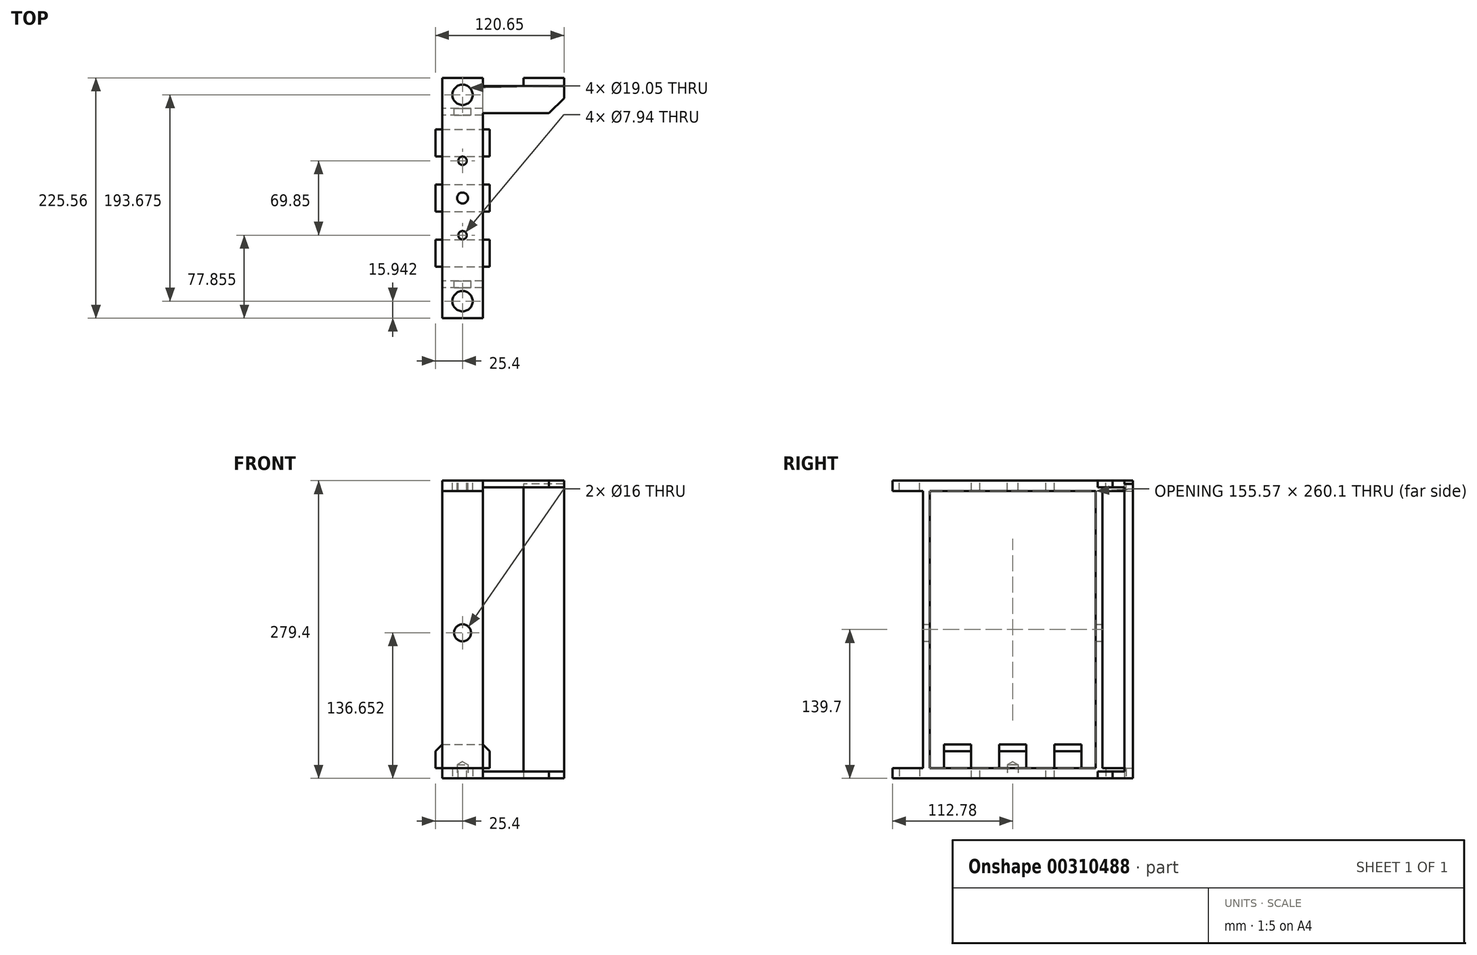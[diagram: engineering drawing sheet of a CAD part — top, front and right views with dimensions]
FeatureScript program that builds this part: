
annotation { "Feature Type Name" : "Feature", "Feature Type Description" : "" }
export const myFeature = defineFeature(function(context is Context, id is Id, definition is map)
    precondition{}
    {
        {
            var Q0;
            Q0=qCreatedBy(makeId("Right.planeOp"),FACE);
            var sketch = newSketch(context, id + "F0", { "sketchPlane" : qUnion([Q0])});
            skLineSegment(sketch, "E0.bottom", {"start": v(-112.78, 139.7) * mm, "end": v(112.78, 139.7) * mm, "construction": true});
            skLineSegment(sketch, "E0.top", {"start": v(-112.78, -139.7) * mm, "end": v(112.78, -139.7) * mm, "construction": true});
            skLineSegment(sketch, "E0.left", {"start": v(-112.78, 139.7) * mm, "end": v(-112.78, -139.7) * mm, "construction": true});
            skLineSegment(sketch, "E0.right", {"start": v(112.78, 139.7) * mm, "end": v(112.78, -139.7) * mm, "construction": true});
            skPoint(sketch, "E0.middle", {"position": v(0, 0) * mm});
            skLineSegment(sketch, "E1.bottom", {"start": v(-112.78, 139.7) * mm, "end": v(112.78, 139.7) * mm});
            skLineSegment(sketch, "E1.top", {"start": v(-112.78, 130.05) * mm, "end": v(112.78, 130.05) * mm});
            skLineSegment(sketch, "E1.left", {"start": v(-112.78, 139.7) * mm, "end": v(-112.78, 130.05) * mm});
            skLineSegment(sketch, "E1.right", {"start": v(112.78, 139.7) * mm, "end": v(112.78, 130.05) * mm});
            skLineSegment(sketch, "E2", {"start": v(-207.6, 0) * mm, "end": v(204.57, 0) * mm, "construction": true});
            skSolve(sketch);
        }
        {
            var Q0;
            Q0=qSketchRegion(id+"F0",true);
            extrude(context, id + "F1", {"entities" : qUnion([Q0]), "endBound" : BoundingType.SYMMETRIC, "depth" : 38.1 * mm});
        }
        {
            var Q0;
            Q0=makeQuery(id+"F1.opExtrude","SWEPT_FACE",FACE,{"disambiguationData":[OSD([sQuery(id+"F0.wireOp",EDGE,"E1.bottom")])]});
            var sketch = newSketch(context, id + "F2", { "sketchPlane" : qUnion([Q0])});
            skLineSegment(sketch, "E3", {"start": v(0, -177.25) * mm, "end": v(0, 167.17) * mm, "construction": true});
            skLineSegment(sketch, "E4", {"start": v(-122.09, 0) * mm, "end": v(96.88, 0) * mm, "construction": true});
            skLineSegment(sketch, "E5.0", {"start": v(-122.09, -96.84) * mm, "end": v(96.88, -96.84) * mm, "construction": true});
            skPoint(sketch, "E6", {"position": v(0, -96.84) * mm});
            skPoint(sketch, "E7.MirrorP", {"position": v(0, 96.84) * mm});
            skSolve(sketch);
        }
        {
            var Q0;
            Q0=sQuery(id+"F2.wireOp",VERTEX,"E6");
            var Q1;
            Q1=sQuery(id+"F2.wireOp",VERTEX,"E7.MirrorP");
            var Q2;
            Q2=makeQuery(id+"F1.opExtrude","SWEPT_BODY",BODY,{"disambiguationData":[OSD([sQuery(id+"F0.wireOp",EDGE,"E1.bottom"),sQuery(id+"F0.wireOp",EDGE,"E1.top"),sQuery(id+"F0.wireOp",EDGE,"E1.left"),sQuery(id+"F0.wireOp",EDGE,"E1.right")])]});
            hole(context, id + "F3", {"style" : HoleStyle.SIMPLE, "endStyle" : HoleEndStyle.THROUGH, "holeDiameter" : 19.05 * mm, "tappedDepth" : 24.13 * mm, "tapClearance" : 3, "startFromSketch" : true, "locations" : qUnion([Q0, Q1]), "scope" : qUnion([Q2])});
        }
        {
            var Q0;
            Q0=makeQuery(id+"F1.opExtrude","SWEPT_BODY",BODY,{"disambiguationData":[OSD([sQuery(id+"F0.wireOp",EDGE,"E1.bottom"),sQuery(id+"F0.wireOp",EDGE,"E1.top"),sQuery(id+"F0.wireOp",EDGE,"E1.left"),sQuery(id+"F0.wireOp",EDGE,"E1.right")])]});
            var Q1;
            Q1=qCreatedBy(makeId("Top.planeOp"),FACE);
            mirror(context, id + "F4", {"entities" : qUnion([Q0]), "mirrorPlane" : qUnion([Q1])});
        }
        {
            var Q0;
            Q0=qCreatedBy(makeId("Right.planeOp"),FACE);
            var sketch = newSketch(context, id + "F5", { "sketchPlane" : qUnion([Q0])});
            skLineSegment(sketch, "E8", {"start": v(0, 150.78) * mm, "end": v(0, -158.23) * mm, "construction": true});
            skLineSegment(sketch, "E9.0", {"start": v(-77.79, 150.78) * mm, "end": v(-77.79, -158.23) * mm, "construction": true});
            skLineSegment(sketch, "E10.0", {"start": v(-112.78, 130.05) * mm, "end": v(112.78, 130.05) * mm, "construction": true});
            skLineSegment(sketch, "E11.0", {"start": v(-112.78, -130.05) * mm, "end": v(112.78, -130.05) * mm, "construction": true});
            skLineSegment(sketch, "E12.bottom", {"start": v(-77.79, 130.05) * mm, "end": v(-84.14, 130.05) * mm});
            skLineSegment(sketch, "E12.top", {"start": v(-77.79, -130.05) * mm, "end": v(-84.14, -130.05) * mm});
            skLineSegment(sketch, "E12.left", {"start": v(-77.79, 130.05) * mm, "end": v(-77.79, -130.05) * mm});
            skLineSegment(sketch, "E12.right", {"start": v(-84.14, 130.05) * mm, "end": v(-84.14, -130.05) * mm});
            skLineSegment(sketch, "E13.MirrorCS", {"start": v(77.79, 130.05) * mm, "end": v(84.14, 130.05) * mm});
            skLineSegment(sketch, "E14.MirrorCS", {"start": v(77.79, -130.05) * mm, "end": v(84.14, -130.05) * mm});
            skLineSegment(sketch, "E15.MirrorCS", {"start": v(77.79, 130.05) * mm, "end": v(77.79, -130.05) * mm});
            skLineSegment(sketch, "E16.MirrorCS", {"start": v(84.14, 130.05) * mm, "end": v(84.14, -130.05) * mm});
            skLineSegment(sketch, "E17.MirrorCS", {"start": v(77.79, 150.78) * mm, "end": v(77.79, -158.23) * mm, "construction": true});
            skSolve(sketch);
        }
        {
            var Q0;
            Q0=qSketchRegion(id+"F5",true);
            extrude(context, id + "F6", {"entities" : qUnion([Q0]), "endBound" : BoundingType.SYMMETRIC, "depth" : 38.1 * mm});
        }
        {
            var Q0;
            Q0=makeQuery(id+"F6.opExtrude","SWEPT_FACE",FACE,{"disambiguationData":[OSD([sQuery(id+"F5.wireOp",EDGE,"E16.MirrorCS")])]});
            var sketch = newSketch(context, id + "F7", { "sketchPlane" : qUnion([Q0])});
            skLineSegment(sketch, "E18.0", {"start": v(-92.9, -130.05) * mm, "end": v(19.05, -130.05) * mm, "construction": true});
            skPoint(sketch, "E19.orphan", {"position": v(-19.05, -130.05) * mm});
            skLineSegment(sketch, "E20", {"start": v(0, 168.5) * mm, "end": v(0, -166.5) * mm, "construction": true});
            skLineSegment(sketch, "E21.0", {"start": v(-92.9, -3.05) * mm, "end": v(19.05, -3.05) * mm, "construction": true});
            skPoint(sketch, "E22", {"position": v(0, -3.05) * mm});
            skSolve(sketch);
        }
        {
            var Q0;
            Q0=makeQuery(id+"F1.opExtrude","SWEPT_BODY",BODY,{"disambiguationData":[OSD([sQuery(id+"F0.wireOp",EDGE,"E1.bottom"),sQuery(id+"F0.wireOp",EDGE,"E1.top"),sQuery(id+"F0.wireOp",EDGE,"E1.left"),sQuery(id+"F0.wireOp",EDGE,"E1.right")])]});
            var Q1;
            Q1=makeQuery(id+"F6.opExtrude","SWEPT_BODY",BODY,{"disambiguationData":[OSD([sQuery(id+"F5.wireOp",EDGE,"E12.bottom"),sQuery(id+"F5.wireOp",EDGE,"E12.top"),sQuery(id+"F5.wireOp",EDGE,"E12.left"),sQuery(id+"F5.wireOp",EDGE,"E12.right")])]});
            var Q2;
            Q2=makeQuery(id+"F6.opExtrude","SWEPT_BODY",BODY,{"disambiguationData":[OSD([sQuery(id+"F5.wireOp",EDGE,"E13.MirrorCS"),sQuery(id+"F5.wireOp",EDGE,"E14.MirrorCS"),sQuery(id+"F5.wireOp",EDGE,"E15.MirrorCS"),sQuery(id+"F5.wireOp",EDGE,"E16.MirrorCS")])]});
            var Q3;
            Q3=makeQuery(id+"F4.opPattern","COPY",BODY,{"derivedFrom":makeQuery(id+"F1.opExtrude","SWEPT_BODY",BODY,{"disambiguationData":[OSD([sQuery(id+"F0.wireOp",EDGE,"E1.bottom"),sQuery(id+"F0.wireOp",EDGE,"E1.top"),sQuery(id+"F0.wireOp",EDGE,"E1.left"),sQuery(id+"F0.wireOp",EDGE,"E1.right")])]}),"instanceName":"1"});
            booleanBodies(context, id + "F8", {"operationType" : BooleanOperationType.UNION, "tools" : qUnion([Q0, Q1, Q2, Q3])});
        }
        {
            var Q0;
            Q0=sQuery(id+"F7.wireOp",VERTEX,"E22");
            var Q1;
            Q1=makeQuery(id+"F1.opExtrude","SWEPT_BODY",BODY,{"disambiguationData":[OSD([sQuery(id+"F0.wireOp",EDGE,"E1.bottom"),sQuery(id+"F0.wireOp",EDGE,"E1.top"),sQuery(id+"F0.wireOp",EDGE,"E1.left"),sQuery(id+"F0.wireOp",EDGE,"E1.right")])]});
            hole(context, id + "F9", {"style" : HoleStyle.SIMPLE, "endStyle" : HoleEndStyle.THROUGH, "holeDiameter" : 16 * mm, "tappedDepth" : 24.13 * mm, "tapClearance" : 3, "startFromSketch" : true, "locations" : qUnion([Q0]), "scope" : qUnion([Q1])});
        }
        {
            var Q0;
            {var subQ2=sQuery(id+"F0.wireOp",EDGE,"E1.top");var subQ7=sQuery(id+"F5.wireOp",EDGE,"E12.left");Q0=makeQuery(id+"F8.opBoolean","SPLIT",FACE,{"disambiguationData":[TD([makeQuery(id+"F6.opExtrude","SWEPT_FACE",FACE,{"disambiguationData":[OSD([subQ7])]})])],"derivedFrom":makeQuery(id+"F4.opPattern","COPY",FACE,{"derivedFrom":makeQuery(id+"F1.opExtrude","SWEPT_FACE",FACE,{"disambiguationData":[OSD([subQ2])]}),"instanceName":"1"})});}
            var sketch = newSketch(context, id + "F10", { "sketchPlane" : qUnion([Q0])});
            skLineSegment(sketch, "E23", {"start": v(-127.69, 0) * mm, "end": v(108.08, 0) * mm, "construction": true});
            skLineSegment(sketch, "E24", {"start": v(0, -187.89) * mm, "end": v(0, 187.89) * mm, "construction": true});
            skLineSegment(sketch, "E25.0", {"start": v(-127.69, -51.69) * mm, "end": v(108.08, -51.69) * mm, "construction": true});
            skLineSegment(sketch, "E26.bottom", {"start": v(-25.4, -64.39) * mm, "end": v(25.4, -64.39) * mm});
            skLineSegment(sketch, "E26.top", {"start": v(-25.4, -38.99) * mm, "end": v(25.4, -38.99) * mm});
            skLineSegment(sketch, "E26.left", {"start": v(-25.4, -64.39) * mm, "end": v(-25.4, -38.99) * mm});
            skLineSegment(sketch, "E26.right", {"start": v(25.4, -64.39) * mm, "end": v(25.4, -38.99) * mm});
            skPoint(sketch, "E26.middle", {"position": v(0, -51.69) * mm});
            skLineSegment(sketch, "E27.0.1.0", {"start": v(-25.4, -12.7) * mm, "end": v(25.4, -12.7) * mm});
            skLineSegment(sketch, "E27.0.1.1", {"start": v(-25.4, 12.7) * mm, "end": v(25.4, 12.7) * mm});
            skLineSegment(sketch, "E27.0.1.2", {"start": v(-25.4, -12.7) * mm, "end": v(-25.4, 12.7) * mm});
            skLineSegment(sketch, "E27.0.1.3", {"start": v(25.4, -12.7) * mm, "end": v(25.4, 12.7) * mm});
            skPoint(sketch, "E27.0.1.4", {"position": v(0, 0) * mm});
            skLineSegment(sketch, "E27.0.2.0", {"start": v(-25.4, 38.99) * mm, "end": v(25.4, 38.99) * mm});
            skLineSegment(sketch, "E27.0.2.1", {"start": v(-25.4, 64.39) * mm, "end": v(25.4, 64.39) * mm});
            skLineSegment(sketch, "E27.0.2.2", {"start": v(-25.4, 38.99) * mm, "end": v(-25.4, 64.39) * mm});
            skLineSegment(sketch, "E27.0.2.3", {"start": v(25.4, 38.99) * mm, "end": v(25.4, 64.39) * mm});
            skPoint(sketch, "E27.0.2.4", {"position": v(0, 51.69) * mm});
            skLineSegment(sketch, "E27.direction1", {"start": v(-25.4, -64.39) * mm, "end": v(0, -64.39) * mm, "construction": true});
            skLineSegment(sketch, "E27.direction2", {"start": v(-25.4, -64.39) * mm, "end": v(-25.4, -12.7) * mm, "construction": true});
            skSolve(sketch);
        }
        {
            var Q0;
            Q0=qSketchRegion(id+"F10",true);
            extrude(context, id + "F11", {"entities" : qUnion([Q0]), "operationType" : NewBodyOperationType.ADD, "depth" : 22.35 * mm});
        }
        {
            var Q0;
            Q0=makeQuery(id+"F11.opExtrude","CAP_EDGE",EDGE,{"disambiguationData":[OSD([sQuery(id+"F10.wireOp",EDGE,"E26.left")])],"isStart":false});
            var Q1;
            Q1=makeQuery(id+"F11.opExtrude","CAP_EDGE",EDGE,{"disambiguationData":[OSD([sQuery(id+"F10.wireOp",EDGE,"E27.0.1.2")])],"isStart":false});
            var Q2;
            Q2=makeQuery(id+"F11.opExtrude","CAP_EDGE",EDGE,{"disambiguationData":[OSD([sQuery(id+"F10.wireOp",EDGE,"E27.0.2.2")])],"isStart":false});
            var Q3;
            Q3=makeQuery(id+"F11.opExtrude","CAP_EDGE",EDGE,{"disambiguationData":[OSD([sQuery(id+"F10.wireOp",EDGE,"E27.0.2.3")])],"isStart":false});
            var Q4;
            Q4=makeQuery(id+"F11.opExtrude","CAP_EDGE",EDGE,{"disambiguationData":[OSD([sQuery(id+"F10.wireOp",EDGE,"E27.0.1.3")])],"isStart":false});
            var Q5;
            Q5=makeQuery(id+"F11.opExtrude","CAP_EDGE",EDGE,{"disambiguationData":[OSD([sQuery(id+"F10.wireOp",EDGE,"E26.right")])],"isStart":false});
            chamfer(context, id + "F12", {"entities" : qUnion([Q0, Q1, Q2, Q3, Q4, Q5]), "width" : 6.35 * mm, "tangentPropagation" : true});
        }
        {
            var Q0;
            Q0=makeQuery(id+"F1.opExtrude","SWEPT_FACE",FACE,{"disambiguationData":[OSD([sQuery(id+"F0.wireOp",EDGE,"E1.bottom")])]});
            var sketch = newSketch(context, id + "F13", { "sketchPlane" : qUnion([Q0])});
            skLineSegment(sketch, "E28", {"start": v(-115.37, 0) * mm, "end": v(101.92, 0) * mm, "construction": true});
            skLineSegment(sketch, "E29", {"start": v(0, -161.57) * mm, "end": v(0, 180.6) * mm, "construction": true});
            skLineSegment(sketch, "E30.0", {"start": v(-115.37, -34.93) * mm, "end": v(101.92, -34.92) * mm, "construction": true});
            skPoint(sketch, "E31", {"position": v(0, -34.93) * mm});
            skPoint(sketch, "E32.MirrorP", {"position": v(0, 34.93) * mm});
            skSolve(sketch);
        }
        {
            var Q0;
            Q0=sQuery(id+"F13.wireOp",VERTEX,"E31");
            var Q1;
            Q1=sQuery(id+"F13.wireOp",VERTEX,"E32.MirrorP");
            var Q2;
            Q2=makeQuery(id+"F1.opExtrude","SWEPT_BODY",BODY,{"disambiguationData":[OSD([sQuery(id+"F0.wireOp",EDGE,"E1.bottom"),sQuery(id+"F0.wireOp",EDGE,"E1.top"),sQuery(id+"F0.wireOp",EDGE,"E1.left"),sQuery(id+"F0.wireOp",EDGE,"E1.right")])]});
            hole(context, id + "F14", {"style" : HoleStyle.SIMPLE, "endStyle" : HoleEndStyle.THROUGH, "standardTappedOrClearance" : lookupTablePath({ "standard" : "ANSI", "engagement" : "75%", "pitch" : "16 tpi", "size" : "3/8", "type" : "Tapped" }), "standardBlindInLast" : lookupTablePath({ "standard" : "ANSI", "engagement" : "75%", "pitch" : "16 tpi", "size" : "3/8", "type" : "Tapped" }), "holeDiameter" : 7.94 * mm, "showTappedDepth" : true, "tappedDepth" : 24.13 * mm, "tapClearance" : 3, "startFromSketch" : true, "locations" : qUnion([Q0, Q1]), "scope" : qUnion([Q2]), "majorDiameter" : 9.53 * mm});
        }
        {
            var Q0;
            Q0=makeQuery(id+"F1.opExtrude","SWEPT_FACE",FACE,{"disambiguationData":[OSD([sQuery(id+"F0.wireOp",EDGE,"E1.bottom")])]});
            var sketch = newSketch(context, id + "F15", { "sketchPlane" : qUnion([Q0])});
            skPoint(sketch, "E33", {"position": v(0, 0) * mm});
            skSolve(sketch);
        }
        {
            var Q0;
            Q0=sQuery(id+"F15.wireOp",VERTEX,"E33");
            var Q1;
            Q1=makeQuery(id+"F1.opExtrude","SWEPT_BODY",BODY,{"disambiguationData":[OSD([sQuery(id+"F0.wireOp",EDGE,"E1.bottom"),sQuery(id+"F0.wireOp",EDGE,"E1.top"),sQuery(id+"F0.wireOp",EDGE,"E1.left"),sQuery(id+"F0.wireOp",EDGE,"E1.right")])]});
            hole(context, id + "F16", {"style" : HoleStyle.SIMPLE, "endStyle" : HoleEndStyle.BLIND, "holeDiameter" : 10.3 * mm, "holeDepth" : 28.9 * mm, "tappedDepth" : 24.13 * mm, "tapClearance" : 3, "startFromSketch" : true, "locations" : qUnion([Q0]), "scope" : qUnion([Q1])});
        }
        {
            var Q0;
            Q0=makeQuery(id+"F4.opPattern","COPY",FACE,{"derivedFrom":makeQuery(id+"F1.opExtrude","SWEPT_FACE",FACE,{"disambiguationData":[OSD([sQuery(id+"F0.wireOp",EDGE,"E1.bottom")])]}),"instanceName":"1"});
            var sketch = newSketch(context, id + "F17", { "sketchPlane" : qUnion([Q0])});
            skPoint(sketch, "E34", {"position": v(0, 0) * mm});
            skSolve(sketch);
        }
        {
            var Q0;
            Q0=sQuery(id+"F17.wireOp",VERTEX,"E34");
            var Q1;
            Q1=makeQuery(id+"F1.opExtrude","SWEPT_BODY",BODY,{"disambiguationData":[OSD([sQuery(id+"F0.wireOp",EDGE,"E1.bottom"),sQuery(id+"F0.wireOp",EDGE,"E1.top"),sQuery(id+"F0.wireOp",EDGE,"E1.left"),sQuery(id+"F0.wireOp",EDGE,"E1.right")])]});
            hole(context, id + "F18", {"style" : HoleStyle.SIMPLE, "endStyle" : HoleEndStyle.BLIND, "holeDiameter" : 10.3 * mm, "holeDepth" : 12.7 * mm, "tappedDepth" : 24.13 * mm, "tapClearance" : 3, "startFromSketch" : true, "locations" : qUnion([Q0]), "scope" : qUnion([Q1])});
        }
        {
            var Q0;
            Q0=makeQuery(id+"F1.opExtrude","SWEPT_FACE",FACE,{"disambiguationData":[OSD([sQuery(id+"F0.wireOp",EDGE,"E1.bottom")])]});
            var sketch = newSketch(context, id + "F19", { "sketchPlane" : qUnion([Q0])});
            skLineSegment(sketch, "E35", {"start": v(-19.05, 112.78) * mm, "end": v(73.29, 112.78) * mm, "construction": true});
            skLineSegment(sketch, "E36.0", {"start": v(-19.05, 104.9) * mm, "end": v(73.29, 104.9) * mm, "construction": true});
            skLineSegment(sketch, "E37.0", {"start": v(-19.05, 79.5) * mm, "end": v(73.29, 79.5) * mm});
            skLineSegment(sketch, "E38.0", {"start": v(19.05, -112.78) * mm, "end": v(19.05, 112.78) * mm, "construction": true});
            skLineSegment(sketch, "E39.bottom", {"start": v(19.05, 79.5) * mm, "end": v(95.25, 79.5) * mm});
            skLineSegment(sketch, "E39.top", {"start": v(19.05, 104.9) * mm, "end": v(95.25, 104.9) * mm});
            skLineSegment(sketch, "E39.left", {"start": v(19.05, 79.5) * mm, "end": v(19.05, 104.9) * mm});
            skLineSegment(sketch, "E39.right", {"start": v(95.25, 79.5) * mm, "end": v(95.25, 104.9) * mm});
            skSolve(sketch);
        }
        {
            var Q0;
            Q0=qSketchRegion(id+"F19",true);
            extrude(context, id + "F20", {"entities" : qUnion([Q0]), "oppositeDirection" : true, "depth" : 6.35 * mm});
        }
        {
            var Q0;
            Q0=makeQuery(id+"F20.opExtrude","SWEPT_BODY",BODY,{"disambiguationData":[OSD([sQuery(id+"F19.wireOp",EDGE,"E39.bottom"),sQuery(id+"F19.wireOp",EDGE,"E39.top"),sQuery(id+"F19.wireOp",EDGE,"E39.left"),sQuery(id+"F19.wireOp",EDGE,"E39.right")])]});
            var Q1;
            Q1=qCreatedBy(makeId("Top.planeOp"),FACE);
            mirror(context, id + "F21", {"operationType" : NewBodyOperationType.ADD, "entities" : qUnion([Q0]), "mirrorPlane" : qUnion([Q1])});
        }
        {
            var Q0;
            Q0=makeQuery(id+"F20.opExtrude","SWEPT_EDGE",EDGE,{"disambiguationData":[OSD([sQuery(id+"F19.wireOp",EDGE,"E39.bottom"),sQuery(id+"F19.wireOp",EDGE,"E39.right")])]});
            var Q1;
            Q1=makeQuery(id+"F21.opPattern","COPY",EDGE,{"derivedFrom":makeQuery(id+"F20.opExtrude","SWEPT_EDGE",EDGE,{"disambiguationData":[OSD([sQuery(id+"F19.wireOp",EDGE,"E39.bottom"),sQuery(id+"F19.wireOp",EDGE,"E39.right")])]}),"instanceName":"1"});
            chamfer(context, id + "F22", {"entities" : qUnion([Q0, Q1]), "width" : 14.22 * mm, "tangentPropagation" : true});
        }
        {
            var Q0;
            Q0=makeQuery(id+"F21.opPattern","COPY",FACE,{"derivedFrom":makeQuery(id+"F20.opExtrude","SWEPT_FACE",FACE,{"disambiguationData":[OSD([sQuery(id+"F19.wireOp",EDGE,"E39.top")])]}),"instanceName":"1"});
            var sketch = newSketch(context, id + "F23", { "sketchPlane" : qUnion([Q0])});
            skLineSegment(sketch, "E40.0", {"start": v(-19.05, -139.7) * mm, "end": v(-95.25, -139.7) * mm, "construction": true});
            skLineSegment(sketch, "E41.0", {"start": v(-19.05, 139.7) * mm, "end": v(-95.25, 139.7) * mm, "construction": true});
            skLineSegment(sketch, "E42.bottom", {"start": v(-95.25, 136.53) * mm, "end": v(-57.15, 136.53) * mm});
            skLineSegment(sketch, "E42.top", {"start": v(-95.25, -139.7) * mm, "end": v(-57.15, -139.7) * mm});
            skLineSegment(sketch, "E42.left", {"start": v(-95.25, 136.53) * mm, "end": v(-95.25, -139.7) * mm});
            skLineSegment(sketch, "E42.right", {"start": v(-57.15, 136.53) * mm, "end": v(-57.15, -139.7) * mm});
            skSolve(sketch);
        }
        {
            var Q0;
            Q0=qSketchRegion(id+"F23",true);
            extrude(context, id + "F24", {"entities" : qUnion([Q0]), "operationType" : NewBodyOperationType.ADD, "depth" : 7.87 * mm});
        }
    });
